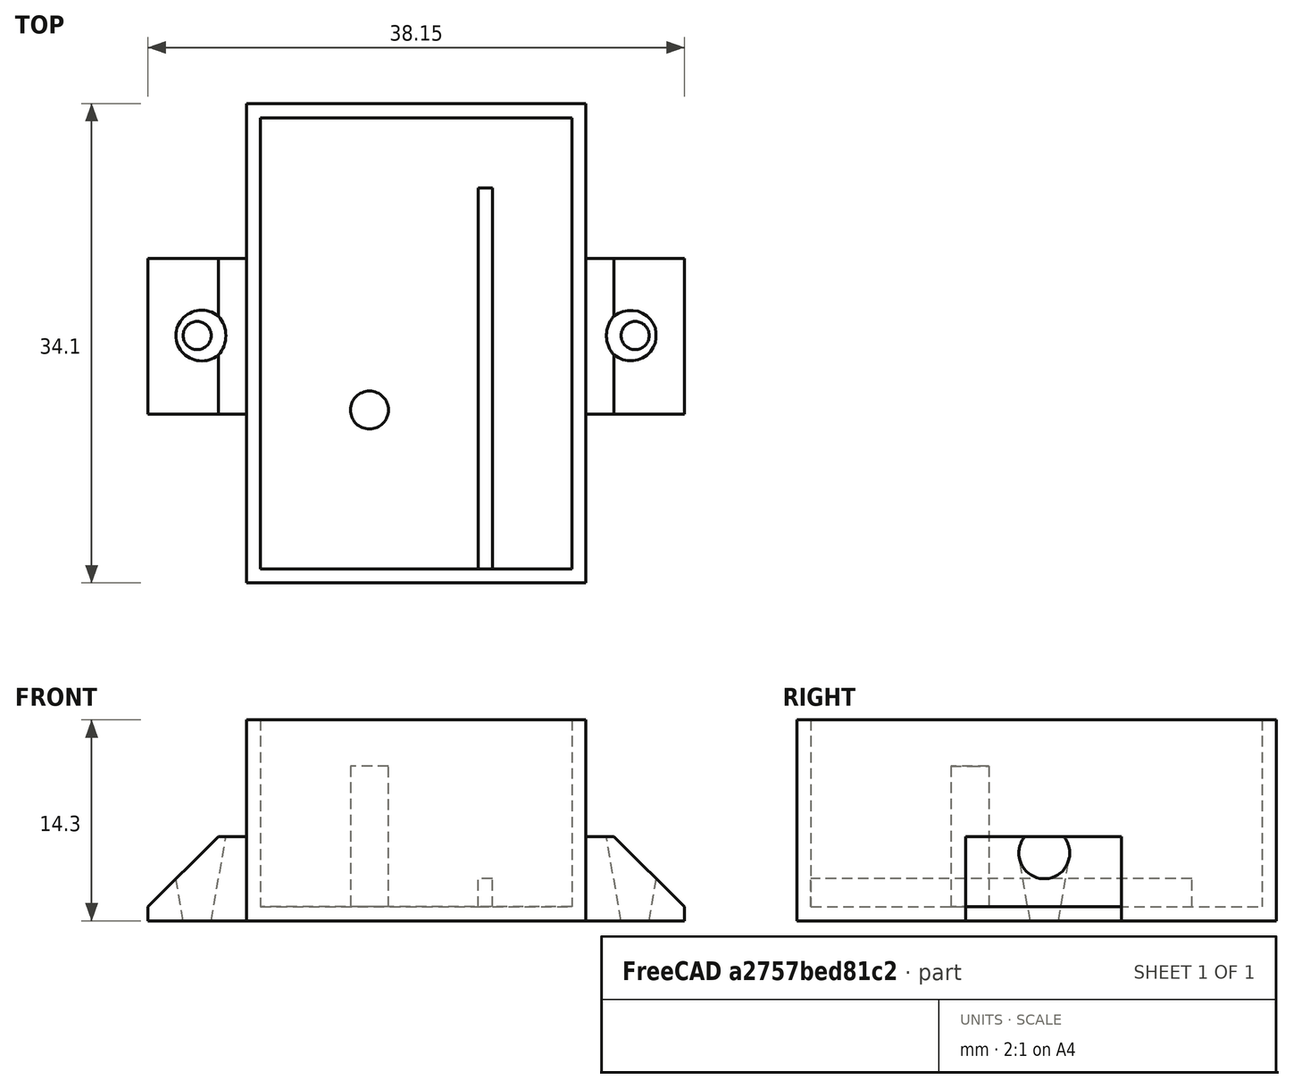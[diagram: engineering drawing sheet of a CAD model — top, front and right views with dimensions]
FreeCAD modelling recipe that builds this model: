
FCSTD DOCUMENT  (FreeCAD 0.18R16117 (Git))
Label: Support switch etagere
License: All rights reserved
LicenseURL: http://en.wikipedia.org/wiki/All_rights_reserved
objects: TechDraw::DrawViewDimension×23, Sketcher::SketchObject×8, PartDesign::Pad×5, TechDraw::DrawViewPart×3, PartDesign::Chamfer×2, PartDesign::Hole×2, Spreadsheet::Sheet×1, PartDesign::Pocket×1, PartDesign::Plane×1, PartDesign::Body×1, TechDraw::DrawSVGTemplate×1, TechDraw::DrawPage×1
note: 28 computed .brp shape members not serialized (recipe doc carries the construction recipe); baked Part::Feature solids carry a one-line shape summary decoded from their .brp

FEATURE [Spreadsheet::Sheet] Spreadsheet
  cells = A2=Bordure ext g; B2=1; A3=Largeur switch; B3=15.6; A4=Marge int; B4==2 * 0.15; A5=Bord int; B5=1; A6=Espace corde; B6=5.25; A7=Bord ext d; B7=1; A8=L max =; B8(Lmax)==sum(B2:B7); A10=Bordure ext h; B10=1; A11=Longueur switch; B11=26.8; A12=Espace fils; B12=5; A13=Marge int; B13==2 * 0.15; A14=Bordure ext b; B14=1; A15=H max =; B15(Hmax)==sum(B10:B14); A17=Fond; B17=1; A18=Prof switch; B18=11; A19=Marge int; B19==2 * 0.15; A20=Espace ; B20=2; A21=P max =; B21(Pmax)==sum(B17:B20)
FEATURE [Sketcher::SketchObject] Sketch
  MapMode = 5
  Support = -> [XY_Plane]
  expr: Constraints[11] = Spreadsheet.Hmax
  expr: Constraints[8] = Spreadsheet.Lmax
  sketch-geometry (4):
    g0: LineSegment StartX=-1 StartY=-1 StartZ=0 EndX=23.15 EndY=-1 EndZ=0
    g1: LineSegment StartX=23.15 StartY=-1 StartZ=0 EndX=23.15 EndY=33.1 EndZ=0
    g2: LineSegment StartX=23.15 StartY=33.1 StartZ=0 EndX=-1 EndY=33.1 EndZ=0
    g3: LineSegment StartX=-1 StartY=33.1 StartZ=0 EndX=-1 EndY=-1 EndZ=0
  constraints (12):
    c: Coincident(g0,g1)
    c: Coincident(g1,g2)
    c: Coincident(g2,g3)
    c: Coincident(g3,g0)
    c: Horizontal(g0)
    c: Horizontal(g2)
    c: Vertical(g1)
    c: Vertical(g3)
    c: DistanceX(g2,g2) = 24.15
    c: DistanceX(g0,g-1) = 1
    c: DistanceY(g0,g-1) = 1
    c: DistanceY(g1,g1) = 34.1
FEATURE [PartDesign::Pad] Pad
  Length = 14.3
  Length2 = 100
  Profile = -> Sketch
  Type = 0
  expr: Length = Spreadsheet.Pmax
FEATURE [Sketcher::SketchObject] Sketch001
  MapMode = 5
  Placement = pos=(0,0,14.3) rot=(0,0,1;0rad)
  Support = -> [Pad]
  expr: Constraints[10] = Spreadsheet.Hmax - 2
  expr: Constraints[9] = Spreadsheet.Lmax - 2
  sketch-geometry (4):
    g0: LineSegment StartX=0 StartY=0 StartZ=0 EndX=22.15 EndY=0 EndZ=0
    g1: LineSegment StartX=22.15 StartY=0 StartZ=0 EndX=22.15 EndY=32.1 EndZ=0
    g2: LineSegment StartX=22.15 StartY=32.1 StartZ=0 EndX=0 EndY=32.1 EndZ=0
    g3: LineSegment StartX=0 StartY=32.1 StartZ=0 EndX=0 EndY=0 EndZ=0
  constraints (11):
    c: Coincident(g0,g1)
    c: Coincident(g1,g2)
    c: Coincident(g2,g3)
    c: Coincident(g3,g0)
    c: Horizontal(g0)
    c: Horizontal(g2)
    c: Vertical(g1)
    c: Vertical(g3)
    c: Coincident(g0,g-1)
    c: DistanceX(g2,g2) = 22.15
    c: DistanceY(g1,g1) = 32.1
FEATURE [PartDesign::Pocket] Pocket
  BaseFeature = -> Pad
  Length = 13.3
  Length2 = 100
  Profile = -> Sketch001
  Type = 0
  expr: Length = Spreadsheet.Pmax - 1
FEATURE [PartDesign::Plane] DatumPlane  label="Referentiel interieur boite"
  Length = 40.7098
  MapMode = 5
  Placement = pos=(0,0,1) rot=(0,0,1;0rad)
  ResizeMode = 0
  Support = -> [Pocket]
  Width = 50.6598
FEATURE [Sketcher::SketchObject] Sketch002
  ExternalGeometry = -> [Pocket]
  MapMode = 5
  Placement = pos=(0,0,1) rot=(0,0,1;0rad)
  Support = -> [Pocket]
  sketch-geometry (4):
    g0: LineSegment StartX=15.5 StartY=27.1 StartZ=0 EndX=16.5 EndY=27.1 EndZ=0
    g1: LineSegment StartX=16.5 StartY=27.1 StartZ=0 EndX=16.5 EndY=0 EndZ=0
    g2: LineSegment StartX=16.5 StartY=0 StartZ=0 EndX=15.5 EndY=0 EndZ=0
    g3: LineSegment StartX=15.5 StartY=0 StartZ=0 EndX=15.5 EndY=27.1 EndZ=0
  constraints (12):
    c: Coincident(g0,g1)
    c: Coincident(g1,g2)
    c: Coincident(g2,g3)
    c: Coincident(g3,g0)
    c: Horizontal(g0)
    c: Horizontal(g2)
    c: Vertical(g1)
    c: Vertical(g3)
    c: DistanceX(g0,g0) = 1
    c: DistanceX(g-1,g2) = 15.5
    c: PointOnObject(g2,g-3)
    c: DistanceY(g1,g1) = 27.1
FEATURE [PartDesign::Pad] Pad001  label="Bord int"
  BaseFeature = -> Pocket
  Length = 2
  Length2 = 100
  Profile = -> Sketch002
  Type = 0
FEATURE [Sketcher::SketchObject] Sketch004
  MapMode = 5
  Placement = pos=(0,0,1) rot=(0,0,1;0rad)
  sketch-geometry (1):
    g0: Circle CenterX=7.75 CenterY=11.3 CenterZ=0 NormalX=0 NormalY=0 NormalZ=1 AngleXU=0 Radius=1.35
  constraints (3):
    c: DistanceY(g-1,g0) = 11.3
    c: DistanceX(g-1,g0) = 7.75
    c: Radius(g0) = 1.35
FEATURE [PartDesign::Pad] Pad003  label="Fix int rond"
  BaseFeature = -> Pad001
  Length = 10
  Length2 = 100
  Profile = -> Sketch004
  Type = 0
FEATURE [Sketcher::SketchObject] Sketch005
  ExternalGeometry = -> [Pad003]
  MapMode = 5
  Placement = pos=(23.15,0,0) rot=(0.57735,0.57735,0.57735;2.0944rad)
  Support = -> [Pad003]
  sketch-geometry (4):
    g0: LineSegment StartX=11 StartY=0 StartZ=0 EndX=22.1 EndY=0 EndZ=0
    g1: LineSegment StartX=22.1 StartY=0 StartZ=0 EndX=22.1 EndY=6 EndZ=0
    g2: LineSegment StartX=22.1 StartY=6 StartZ=0 EndX=11 EndY=6 EndZ=0
    g3: LineSegment StartX=11 StartY=6 StartZ=0 EndX=11 EndY=0 EndZ=0
  constraints (12):
    c: Coincident(g0,g1)
    c: Coincident(g1,g2)
    c: Coincident(g2,g3)
    c: Coincident(g3,g0)
    c: Horizontal(g0)
    c: Horizontal(g2)
    c: Vertical(g1)
    c: Vertical(g3)
    c: DistanceX(g-1,g0) = 11
    c: DistanceX(g0,g-3) = 11
    c: PointOnObject(g0,g-1)
    c: DistanceY(g1,g1) = 6
FEATURE [PartDesign::Pad] Pad004  label="Pad d"
  BaseFeature = -> Pad003
  Length = 7
  Length2 = 100
  Profile = -> Sketch005
  Type = 0
FEATURE [PartDesign::Chamfer] Chamfer  label="Chamfer d"
  Base = -> Pad004 [Edge26]
  BaseFeature = -> Pad004
  Size = 5
FEATURE [Sketcher::SketchObject] Sketch006
  ExternalGeometry = -> [Chamfer]
  MapMode = 5
  Placement = pos=(-1,0,0) rot=(0.57735,-0.57735,-0.57735;2.0944rad)
  Support = -> [Chamfer]
  sketch-geometry (4):
    g0: LineSegment StartX=-11 StartY=0 StartZ=0 EndX=-22.1 EndY=0 EndZ=0
    g1: LineSegment StartX=-22.1 StartY=0 StartZ=0 EndX=-22.1 EndY=6 EndZ=0
    g2: LineSegment StartX=-22.1 StartY=6 StartZ=0 EndX=-11 EndY=6 EndZ=0
    g3: LineSegment StartX=-11 StartY=6 StartZ=0 EndX=-11 EndY=0 EndZ=0
  constraints (12):
    c: Coincident(g0,g1)
    c: Coincident(g1,g2)
    c: Coincident(g2,g3)
    c: Coincident(g3,g0)
    c: Horizontal(g0)
    c: Horizontal(g2)
    c: Vertical(g1)
    c: Vertical(g3)
    c: DistanceX(g0,g-1) = 11
    c: DistanceX(g-3,g0) = 11
    c: PointOnObject(g0,g-1)
    c: DistanceY(g3,g3) = 6
FEATURE [PartDesign::Pad] Pad005  label="Pad g"
  BaseFeature = -> Chamfer
  Length = 7
  Length2 = 100
  Profile = -> Sketch006
  Type = 0
FEATURE [PartDesign::Chamfer] Chamfer001  label="Chamfer g"
  Base = -> Pad005 [Edge56]
  BaseFeature = -> Pad005
  Size = 5
FEATURE [Sketcher::SketchObject] Sketch008
  ExternalGeometry = -> [Chamfer001]
  MapMode = 5
  Placement = pos=(0,0,0) rot=(1,0,0;3.14159rad)
  Support = -> [Chamfer001]
  sketch-geometry (1):
    g0: Circle CenterX=-4.5 CenterY=-16.6 CenterZ=0 NormalX=0 NormalY=0 NormalZ=1 AngleXU=0 Radius=2.1
  constraints (3):
    c: DistanceX(g-4,g0) = 3.5
    c: DistanceY(g-4,g0) = 5.5
    c: Radius(g0) = 2.1
FEATURE [PartDesign::Hole] Hole  label="Percage d"
  BaseFeature = -> Chamfer001
  Depth = 25
  DepthType = 0
  Diameter = 2
  DrillPoint = 1
  DrillPointAngle = 118
  HoleCutCountersinkAngle = 90
  HoleCutDepth = 0
  HoleCutDiameter = 0
  HoleCutType = 0
  ModelActualThread = false
  Profile = -> Sketch008
  Tapered = true
  TaperedAngle = 100
  ThreadAngle = 0
  ThreadClass = 0
  ThreadCutOffInner = 0
  ThreadCutOffOuter = 0
  ThreadDirection = 0
  ThreadFit = 0
  ThreadPitch = 0
  ThreadSize = 0
  ThreadType = 0
  Threaded = false
FEATURE [Sketcher::SketchObject] Sketch009
  ExternalGeometry = -> [Hole]
  MapMode = 5
  Placement = pos=(0,0,0) rot=(1,0,0;3.14159rad)
  Support = -> [Hole]
  sketch-geometry (1):
    g0: Circle CenterX=26.65 CenterY=-16.6 CenterZ=0 NormalX=0 NormalY=0 NormalZ=1 AngleXU=0 Radius=2.1
  constraints (3):
    c: DistanceX(g0,g-4) = 3.5
    c: DistanceY(g-4,g0) = 5.5
    c: Radius(g0) = 2.1
FEATURE [PartDesign::Hole] Hole001  label="Percage g"
  BaseFeature = -> Hole
  Depth = 25
  DepthType = 0
  Diameter = 2
  DrillPoint = 1
  DrillPointAngle = 118
  HoleCutCountersinkAngle = 90
  HoleCutDepth = 0
  HoleCutDiameter = 0
  HoleCutType = 0
  ModelActualThread = false
  Profile = -> Sketch009
  Tapered = true
  TaperedAngle = 100
  ThreadAngle = 0
  ThreadClass = 0
  ThreadCutOffInner = 0
  ThreadCutOffOuter = 0
  ThreadDirection = 0
  ThreadFit = 0
  ThreadPitch = 0
  ThreadSize = 0
  ThreadType = 0
  Threaded = false
FEATURE [PartDesign::Body] Body  label="Support boite"
  Group = -> [Sketch,Pad,Sketch001,Pocket,DatumPlane,Sketch002,Pad001,Sketch004,Pad003,Sketch005,Pad004,Chamfer,Sketch006,Pad005,Chamfer001,Sketch008,Hole,Sketch009,Hole001]
  Origin = -> Origin
  Tip = -> Hole001
FEATURE [TechDraw::DrawSVGTemplate] Template
  EditableTexts = Designed_by_Name=Designed by Name; Drawing_number=Drawing number; FC-Date=11/2019; FC-SC=Scale; FC-SH=Sheet; FC-Title=Support interrupteur etagère LED; Subtitle=Subtitle; Weight=Weight
  Height = 210
  Orientation = 1
  Width = 297
FEATURE [TechDraw::DrawViewPart] View
  CoarseView = false
  Direction = (0,0,1)
  Focus = 100
  HardHidden = false
  IsoCount = 0
  IsoHidden = false
  IsoVisible = false
  LockPosition = false
  Perspective = false
  Rotation = 0
  Scale = 3
  ScaleType = 0
  SeamHidden = false
  SeamVisible = false
  SmoothHidden = false
  SmoothVisible = false
  Source = -> [Hole001]
  X = 89.9614
  Y = 119.149
FEATURE [TechDraw::DrawViewDimension] Dimension
  Arbitrary = false
  FormatSpec = %.2f
  LockPosition = false
  MeasureType = 1
  OverTolerance = 0
  References2D = -> [View]
  Rotation = 0
  ScaleType = 0
  Type = 2
  UnderTolerance = 0
  X = 1.59548
  Y = -30.8001
FEATURE [TechDraw::DrawViewDimension] Dimension001
  Arbitrary = false
  FormatSpec = %.2f
  LockPosition = false
  MeasureType = 1
  OverTolerance = 0
  References2D = -> [View]
  Rotation = 0
  ScaleType = 0
  Type = 1
  UnderTolerance = 0
  X = 4.04336
  Y = 59.3094
FEATURE [TechDraw::DrawViewDimension] Dimension002
  Arbitrary = false
  FormatSpec = %.2f
  LockPosition = false
  MeasureType = 1
  OverTolerance = 0
  References2D = -> [View]
  Rotation = 0
  ScaleType = 0
  Type = 1
  UnderTolerance = 0
  X = 4.94717
  Y = 66.9701
FEATURE [TechDraw::DrawViewDimension] Dimension003
  Arbitrary = false
  FormatSpec = %.2f
  LockPosition = false
  MeasureType = 1
  OverTolerance = 0
  References2D = -> [View]
  Rotation = 0
  ScaleType = 0
  Type = 2
  UnderTolerance = 0
  X = 70.284
  Y = -1.58563
FEATURE [TechDraw::DrawViewDimension] Dimension004
  Arbitrary = false
  FormatSpec = %.2f
  LockPosition = false
  MeasureType = 1
  OverTolerance = 0
  References2D = -> [View]
  Rotation = 0
  ScaleType = 0
  Type = 2
  UnderTolerance = 0
  X = 62.3141
  Y = -20.3754
FEATURE [TechDraw::DrawViewDimension] Dimension005
  Arbitrary = false
  FormatSpec = %.2f
  LockPosition = false
  MeasureType = 1
  OverTolerance = 0
  References2D = -> [View]
  Rotation = 0
  ScaleType = 0
  Type = 2
  UnderTolerance = 0
  X = -66.8658
  Y = 3.13267
FEATURE [TechDraw::DrawViewDimension] Dimension006
  Arbitrary = false
  FormatSpec = %.2f
  LockPosition = false
  MeasureType = 1
  OverTolerance = 0
  References2D = -> [View]
  Rotation = 0
  ScaleType = 0
  Type = 1
  UnderTolerance = 0
  X = -47.26
  Y = 32.5784
FEATURE [TechDraw::DrawViewDimension] Dimension007
  Arbitrary = false
  FormatSpec = ⌀%.2f
  LockPosition = false
  MeasureType = 1
  OverTolerance = 0
  References2D = -> [View]
  Rotation = 0
  ScaleType = 0
  Type = 5
  UnderTolerance = 0
  X = -66.0495
  Y = -20.9779
FEATURE [TechDraw::DrawViewDimension] Dimension008
  Arbitrary = false
  FormatSpec = ⌀%.2f
  LockPosition = false
  MeasureType = 1
  OverTolerance = 0
  References2D = -> [View]
  Rotation = 0
  ScaleType = 0
  Type = 5
  UnderTolerance = 0
  X = -5.481
  Y = 1.05445
FEATURE [TechDraw::DrawViewDimension] Dimension009
  Arbitrary = false
  FormatSpec = %.2f
  LockPosition = false
  MeasureType = 1
  OverTolerance = 0
  References2D = -> [View]
  Rotation = 0
  ScaleType = 0
  Type = 1
  UnderTolerance = 0
  X = -8.66243
  Y = -58.0092
FEATURE [TechDraw::DrawViewDimension] Dimension010
  Arbitrary = false
  FormatSpec = %.2f
  LockPosition = false
  MeasureType = 1
  OverTolerance = 0
  References2D = -> [View]
  Rotation = 0
  ScaleType = 0
  Type = 1
  UnderTolerance = 0
  X = -19.585
  Y = -37.502
FEATURE [TechDraw::DrawViewDimension] Dimension011
  Arbitrary = false
  FormatSpec = %.2f
  LockPosition = false
  MeasureType = 1
  OverTolerance = 0
  References2D = -> [View]
  Rotation = 0
  ScaleType = 0
  Type = 1
  UnderTolerance = 0
  X = 0.55687
  Y = 41.9173
FEATURE [TechDraw::DrawViewDimension] Dimension012
  Arbitrary = false
  FormatSpec = %.2f
  LockPosition = false
  MeasureType = 1
  OverTolerance = 0
  References2D = -> [View]
  Rotation = 0
  ScaleType = 0
  Type = 2
  UnderTolerance = 0
  X = 21.6979
  Y = -8.64166
FEATURE [TechDraw::DrawViewPart] View001
  CoarseView = false
  Direction = (0,-1,0)
  Focus = 100
  HardHidden = false
  IsoCount = 0
  IsoHidden = false
  IsoVisible = false
  LockPosition = false
  Perspective = false
  Rotation = 0
  Scale = 2
  ScaleType = 0
  SeamHidden = false
  SeamVisible = false
  SmoothHidden = false
  SmoothVisible = false
  Source = -> [Hole001]
  X = 226.872
  Y = 158.906
FEATURE [TechDraw::DrawViewDimension] Dimension013
  Arbitrary = false
  FormatSpec = %.2f
  LockPosition = false
  MeasureType = 1
  OverTolerance = 0
  References2D = -> [View001]
  Rotation = 0
  ScaleType = 0
  Type = 1
  UnderTolerance = 0
  X = -1.92391
  Y = -21.5715
FEATURE [TechDraw::DrawViewDimension] Dimension014
  Arbitrary = false
  FormatSpec = %.2f
  LockPosition = false
  MeasureType = 1
  OverTolerance = 0
  References2D = -> [View001]
  Rotation = 0
  ScaleType = 0
  Type = 2
  UnderTolerance = 0
  X = 46.7453
  Y = -0.237845
FEATURE [TechDraw::DrawViewDimension] Dimension015
  Arbitrary = false
  FormatSpec = %.2f
  LockPosition = false
  MeasureType = 1
  OverTolerance = 0
  References2D = -> [View001]
  Rotation = 0
  ScaleType = 0
  Type = 2
  UnderTolerance = 0
  X = -52.8911
  Y = 16.198
FEATURE [TechDraw::DrawViewDimension] Dimension016
  Arbitrary = false
  FormatSpec = %.2f
  LockPosition = false
  MeasureType = 1
  OverTolerance = 0
  References2D = -> [View001]
  Rotation = 0
  ScaleType = 0
  Type = 1
  UnderTolerance = 0
  X = 33.7663
  Y = 28.2742
FEATURE [TechDraw::DrawViewDimension] Dimension017
  Arbitrary = false
  FormatSpec = %.2f
  LockPosition = false
  MeasureType = 1
  OverTolerance = 0
  References2D = -> [View001]
  Rotation = 0
  ScaleType = 0
  Type = 1
  UnderTolerance = 0
  X = 0.237845
  Y = 9.06742
FEATURE [TechDraw::DrawViewPart] View002
  CoarseView = false
  Direction = (1,0,0)
  Focus = 100
  HardHidden = false
  IsoCount = 0
  IsoHidden = false
  IsoVisible = false
  LockPosition = false
  Perspective = false
  Rotation = 0
  Scale = 2
  ScaleType = 0
  SeamHidden = false
  SeamVisible = false
  SmoothHidden = false
  SmoothVisible = false
  Source = -> [Hole001]
  X = 227.62
  Y = 89.9335
FEATURE [TechDraw::DrawViewDimension] Dimension018
  Arbitrary = false
  FormatSpec = %.2f
  LockPosition = false
  MeasureType = 1
  OverTolerance = 0
  References2D = -> [View002]
  Rotation = 0
  ScaleType = 0
  Type = 1
  UnderTolerance = 0
  X = 1.08561
  Y = 23.6362
FEATURE [TechDraw::DrawViewDimension] Dimension019
  Arbitrary = false
  FormatSpec = %.2f
  LockPosition = false
  MeasureType = 1
  OverTolerance = 0
  References2D = -> [View002]
  Rotation = 0
  ScaleType = 0
  Type = 2
  UnderTolerance = 0
  X = 40.3965
  Y = -0.434243
FEATURE [TechDraw::DrawViewDimension] Dimension020
  Arbitrary = false
  FormatSpec = %.2f
  LockPosition = false
  MeasureType = 1
  OverTolerance = 0
  References2D = -> [View002]
  Rotation = 0
  ScaleType = 0
  Type = 1
  UnderTolerance = 0
  X = -21.4486
  Y = -23.202
FEATURE [TechDraw::DrawViewDimension] Dimension021
  Arbitrary = false
  FormatSpec = %.2f
  LockPosition = false
  MeasureType = 1
  OverTolerance = 0
  References2D = -> [View002]
  Rotation = 0
  ScaleType = 0
  Type = 1
  UnderTolerance = 0
  X = 3.60546
  Y = -23.4191
FEATURE [TechDraw::DrawViewDimension] Dimension022
  Arbitrary = false
  FormatSpec = %.2f
  LockPosition = false
  MeasureType = 1
  OverTolerance = 0
  References2D = -> [View002]
  Rotation = 0
  ScaleType = 0
  Type = 1
  UnderTolerance = 0
  X = 27.8767
  Y = -23.6362
FEATURE [TechDraw::DrawPage] Page
  KeepUpdated = true
  ProjectionType = 0
  Template = -> Template
  Views = -> [View,Dimension,Dimension001,Dimension002,Dimension003,Dimension004,Dimension005,Dimension006,Dimension007,Dimension008,Dimension009,Dimension010,Dimension011,Dimension012,View001,Dimension013,Dimension014,Dimension015,Dimension016,Dimension017,View002,Dimension018,Dimension019,Dimension020,Dimension021,Dimension022]
